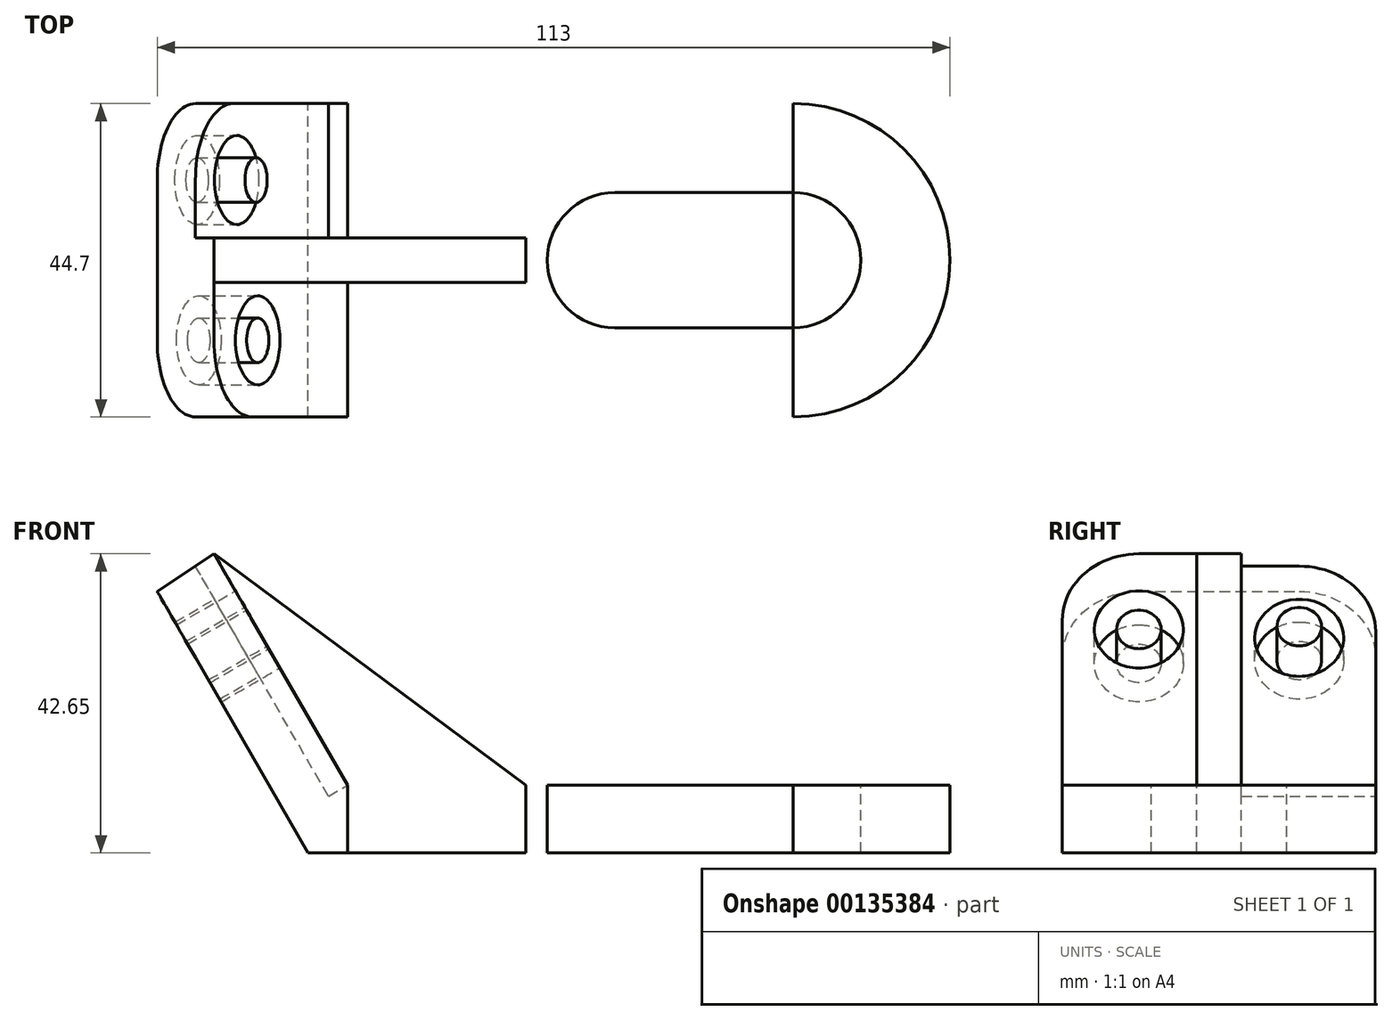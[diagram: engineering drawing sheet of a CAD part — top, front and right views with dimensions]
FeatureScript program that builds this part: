
annotation { "Feature Type Name" : "Feature", "Feature Type Description" : "" }
export const myFeature = defineFeature(function(context is Context, id is Id, definition is map)
    precondition{}
    {
        {
            var Q0;
            Q0=qCreatedBy(makeId("Front.planeOp"),FACE);
            var sketch = newSketch(context, id + "F0", { "sketchPlane" : qUnion([Q0])});
            skLineSegment(sketch, "E0", {"start": v(-33.44, 0) * mm, "end": v(30.06, 0) * mm});
            skLineSegment(sketch, "E1", {"start": v(30.06, -9.65) * mm, "end": v(-39.06, -9.65) * mm});
            skLineSegment(sketch, "E2", {"start": v(-33.44, 0) * mm, "end": v(-52.49, 33) * mm});
            skLineSegment(sketch, "E3", {"start": v(-39.06, -9.65) * mm, "end": v(-60.58, 27.63) * mm});
            skLineSegment(sketch, "E4", {"start": v(-60.58, 27.63) * mm, "end": v(-52.49, 33) * mm});
            skLineSegment(sketch, "E5", {"start": v(30.06, 0) * mm, "end": v(30.06, -9.65) * mm});
            skLineSegment(sketch, "E6", {"start": v(-33.44, 0) * mm, "end": v(-8.04, 0) * mm});
            skLineSegment(sketch, "E7", {"start": v(-52.49, 33) * mm, "end": v(-8.04, 0) * mm});
            skSolve(sketch);
        }
        {
            var Q0;
            Q0=makeQuery(id+"F0.imprint","IMPRINT",FACE,{"disambiguationData":[TD([[makeQuery(id+"F0.imprint","IMPRINT",EDGE,{"derivedFrom":sQuery(id+"F0.wireOp",EDGE,"E0")}),-1.0]])]});
            extrude(context, id + "F1", {"entities" : qUnion([Q0]), "endBound" : BoundingType.SYMMETRIC, "depth" : 44.7 * mm});
        }
        {
            var Q0;
            Q0=makeQuery(id+"F0.imprint","IMPRINT",FACE,{"disambiguationData":[TD([[makeQuery(id+"F0.imprint","IMPRINT",EDGE,{"derivedFrom":sQuery(id+"F0.wireOp",EDGE,"E2")}),-1.0]])]});
            extrude(context, id + "F2", {"entities" : qUnion([Q0]), "operationType" : NewBodyOperationType.ADD, "endBound" : BoundingType.SYMMETRIC, "oppositeDirection" : true, "depth" : 6.35 * mm});
        }
        {
            var Q0;
            Q0=makeQuery(id+"F1.opExtrude","CAP_EDGE",EDGE,{"disambiguationData":[OSD([sQuery(id+"F0.wireOp",EDGE,"E4")])],"isStart":false});
            var Q1;
            Q1=makeQuery(id+"F1.opExtrude","CAP_EDGE",EDGE,{"disambiguationData":[OSD([sQuery(id+"F0.wireOp",EDGE,"E4")])],"isStart":true});
            fillet(context, id + "F3", {"entities" : qUnion([Q0, Q1]), "radius" : 10.92 * mm, "tangentPropagation" : true, "allowEdgeOverflow" : false});
        }
        {
            var Q0;
            Q0=makeQuery(id+"F1.opExtrude","SWEPT_FACE",FACE,{"disambiguationData":[OSD([sQuery(id+"F0.wireOp",EDGE,"E0"),sQuery(id+"F0.wireOp",EDGE,"E6")])]});
            var sketch = newSketch(context, id + "F4", { "sketchPlane" : qUnion([Q0])});
            skArc(sketch, "E8", {"start": v(30.06, -22.35) * mm, "mid": v(52.42, 0) * mm, "end": v(30.06, 22.35) * mm});
            skLineSegment(sketch, "E9", {"start": v(4.66, 0) * mm, "end": v(30.06, 0) * mm});
            skArc(sketch, "E10.0.startCap", {"start": v(4.66, -9.65) * mm, "mid": v(-4.99, 0) * mm, "end": v(4.66, 9.65) * mm});
            skArc(sketch, "E10.0.endCap", {"start": v(30.06, 9.65) * mm, "mid": v(39.72, 0) * mm, "end": v(30.06, -9.65) * mm});
            skLineSegment(sketch, "E10.0.left", {"start": v(4.66, 9.65) * mm, "end": v(30.06, 9.65) * mm});
            skLineSegment(sketch, "E10.0.right", {"start": v(4.66, -9.65) * mm, "end": v(30.06, -9.65) * mm});
            skSolve(sketch);
        }
        {
            var Q0;
            {var subQ0=sQuery(id+"F4.wireOp",EDGE,"E8");Q0=makeQuery(id+"F4.imprint","IMPRINT",FACE,{"disambiguationData":[TD([[makeQuery(id+"F4.imprint","IMPRINT",EDGE,{"derivedFrom":subQ0}),1.0]])]});}
            extrude(context, id + "F5", {"entities" : qUnion([Q0]), "operationType" : NewBodyOperationType.ADD, "oppositeDirection" : true, "depth" : 9.65 * mm});
        }
        {
            var Q0;
            Q0=makeQuery(id+"F4.imprint","IMPRINT",FACE,{"disambiguationData":[TD([[makeQuery(id+"F4.imprint","IMPRINT",EDGE,{"derivedFrom":sQuery(id+"F4.wireOp",EDGE,"E10.0.startCap")}),-1.0]])]});
            extrude(context, id + "F6", {"entities" : qUnion([Q0]), "operationType" : NewBodyOperationType.REMOVE, "oppositeDirection" : true, "depth" : 9.65 * mm});
        }
        {
            var Q0;
            Q0=makeQuery(id+"F1.opExtrude","SWEPT_FACE",FACE,{"disambiguationData":[OSD([sQuery(id+"F0.wireOp",EDGE,"E3")])]});
            var sketch = newSketch(context, id + "F7", { "sketchPlane" : qUnion([Q0])});
            skCircle(sketch, "E11", {"center": v(-11.44, 42.82) * mm, "radius": 6.35 * mm});
            skCircle(sketch, "E12", {"center": v(11.42, 42.36) * mm, "radius": 6.35 * mm});
            skCircle(sketch, "E13", {"center": v(-11.44, 42.82) * mm, "radius": 3.18 * mm});
            skCircle(sketch, "E14", {"center": v(11.42, 42.36) * mm, "radius": 3.18 * mm});
            skSolve(sketch);
        }
        {
            var Q0;
            {var subQ0=sQuery(id+"F0.wireOp",EDGE,"E7");var subQ1=sQuery(id+"F0.wireOp",EDGE,"E6");var subQ2=sQuery(id+"F0.wireOp",EDGE,"E2");Q0=makeQuery(id+"F2.boolean.opBoolean","SPLIT",FACE,{"disambiguationData":[TD([makeQuery(id+"F2.opExtrude","CAP_FACE",FACE,{"disambiguationData":[OSD([subQ2,subQ1,subQ0])],"isStart":false})])],"derivedFrom":makeQuery(id+"F1.opExtrude","SWEPT_FACE",FACE,{"disambiguationData":[OSD([subQ2])]})});}
            var sketch = newSketch(context, id + "F8", { "sketchPlane" : qUnion([Q0])});
            skCircle(sketch, "E15.0", {"center": v(-11.42, 42.36) * mm, "radius": 6.35 * mm});
            skCircle(sketch, "E16.0", {"center": v(11.44, 42.82) * mm, "radius": 6.35 * mm});
            skCircle(sketch, "E17.0", {"center": v(-11.42, 42.36) * mm, "radius": 3.18 * mm});
            skCircle(sketch, "E18.0", {"center": v(11.44, 42.82) * mm, "radius": 3.18 * mm});
            skSolve(sketch);
        }
        {
            var Q0;
            Q0=makeQuery(id+"F8.imprint","IMPRINT",FACE,{"disambiguationData":[TD([[makeQuery(id+"F8.imprint","IMPRINT",EDGE,{"derivedFrom":sQuery(id+"F8.wireOp",EDGE,"E17.0")}),-1.0]])]});
            var Q1;
            Q1=makeQuery(id+"F8.imprint","IMPRINT",FACE,{"disambiguationData":[TD([[makeQuery(id+"F8.imprint","IMPRINT",EDGE,{"derivedFrom":sQuery(id+"F8.wireOp",EDGE,"E18.0")}),-1.0]])]});
            extrude(context, id + "F9", {"entities" : qUnion([Q0, Q1]), "operationType" : NewBodyOperationType.REMOVE, "oppositeDirection" : true, "depth" : 22.35 * mm});
        }
        {
            var Q0;
            Q0=makeQuery(id+"F8.imprint","IMPRINT",FACE,{"disambiguationData":[TD([[makeQuery(id+"F8.imprint","IMPRINT",EDGE,{"derivedFrom":sQuery(id+"F8.wireOp",EDGE,"E15.0")}),-1.0]])]});
            var Q1;
            Q1=makeQuery(id+"F8.imprint","IMPRINT",FACE,{"disambiguationData":[TD([[makeQuery(id+"F8.imprint","IMPRINT",EDGE,{"derivedFrom":sQuery(id+"F8.wireOp",EDGE,"E16.0")}),-1.0]])]});
            extrude(context, id + "F10", {"entities" : qUnion([Q0, Q1]), "operationType" : NewBodyOperationType.REMOVE, "oppositeDirection" : true, "depth" : 3.17 * mm});
        }
    });
